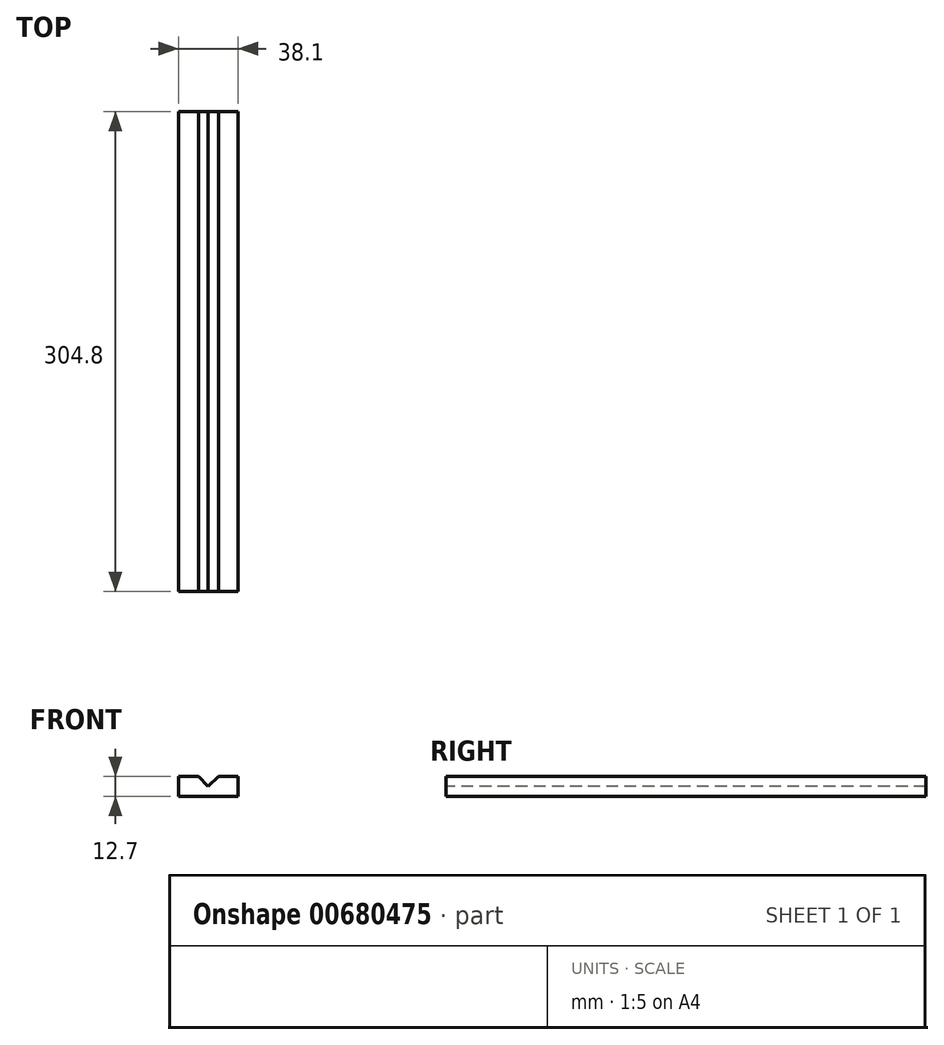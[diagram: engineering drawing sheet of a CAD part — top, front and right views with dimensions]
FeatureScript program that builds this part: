
annotation { "Feature Type Name" : "Feature", "Feature Type Description" : "" }
export const myFeature = defineFeature(function(context is Context, id is Id, definition is map)
    precondition{}
    {
        {
            var Q0;
            Q0=qCreatedBy(makeId("Front.planeOp"),FACE);
            var sketch = newSketch(context, id + "F0", { "sketchPlane" : qUnion([Q0])});
            skLineSegment(sketch, "E0.bottom", {"start": v(19.05, 6.35) * mm, "end": v(-19.05, 6.35) * mm});
            skLineSegment(sketch, "E0.top", {"start": v(19.05, -6.35) * mm, "end": v(-19.05, -6.35) * mm});
            skLineSegment(sketch, "E0.left", {"start": v(19.05, 6.35) * mm, "end": v(19.05, -6.35) * mm});
            skLineSegment(sketch, "E0.right", {"start": v(-19.05, 6.35) * mm, "end": v(-19.05, -6.35) * mm});
            skPoint(sketch, "E0.middle", {"position": v(0, 0) * mm});
            skSolve(sketch);
        }
        {
            var Q0;
            Q0=makeQuery(id+"F0.imprint","IMPRINT",FACE,{"disambiguationData":[TD([[makeQuery(id+"F0.imprint","IMPRINT",EDGE,{"derivedFrom":sQuery(id+"F0.wireOp",EDGE,"E0.bottom")}),1.0]])]});
            extrude(context, id + "F1", {"entities" : qUnion([Q0]), "depth" : 304.8 * mm, "offsetDistance" : 25 * mm});
        }
        {
            var Q0;
            Q0=makeQuery(id+"F1.opExtrude","CAP_FACE",FACE,{"disambiguationData":[OSD([sQuery(id+"F0.wireOp",EDGE,"E0.bottom"),sQuery(id+"F0.wireOp",EDGE,"E0.top"),sQuery(id+"F0.wireOp",EDGE,"E0.left"),sQuery(id+"F0.wireOp",EDGE,"E0.right")])],"isStart":false});
            var sketch = newSketch(context, id + "F2", { "sketchPlane" : qUnion([Q0])});
            skLineSegment(sketch, "E1", {"start": v(0, 0) * mm, "end": v(6.35, 6.35) * mm});
            skLineSegment(sketch, "E2", {"start": v(6.35, 6.35) * mm, "end": v(-6.35, 6.35) * mm});
            skLineSegment(sketch, "E3", {"start": v(-6.35, 6.35) * mm, "end": v(0, 0) * mm});
            skSolve(sketch);
        }
        {
            var Q0;
            Q0=makeQuery(id+"F2.imprint","IMPRINT",FACE,{"disambiguationData":[TD([[makeQuery(id+"F2.imprint","IMPRINT",EDGE,{"derivedFrom":sQuery(id+"F2.wireOp",EDGE,"E1")}),1.0]])]});
            extrude(context, id + "F3", {"entities" : qUnion([Q0]), "operationType" : NewBodyOperationType.REMOVE, "endBound" : BoundingType.THROUGH_ALL, "oppositeDirection" : true, "depth" : 25 * mm, "offsetDistance" : 25 * mm});
        }
    });
